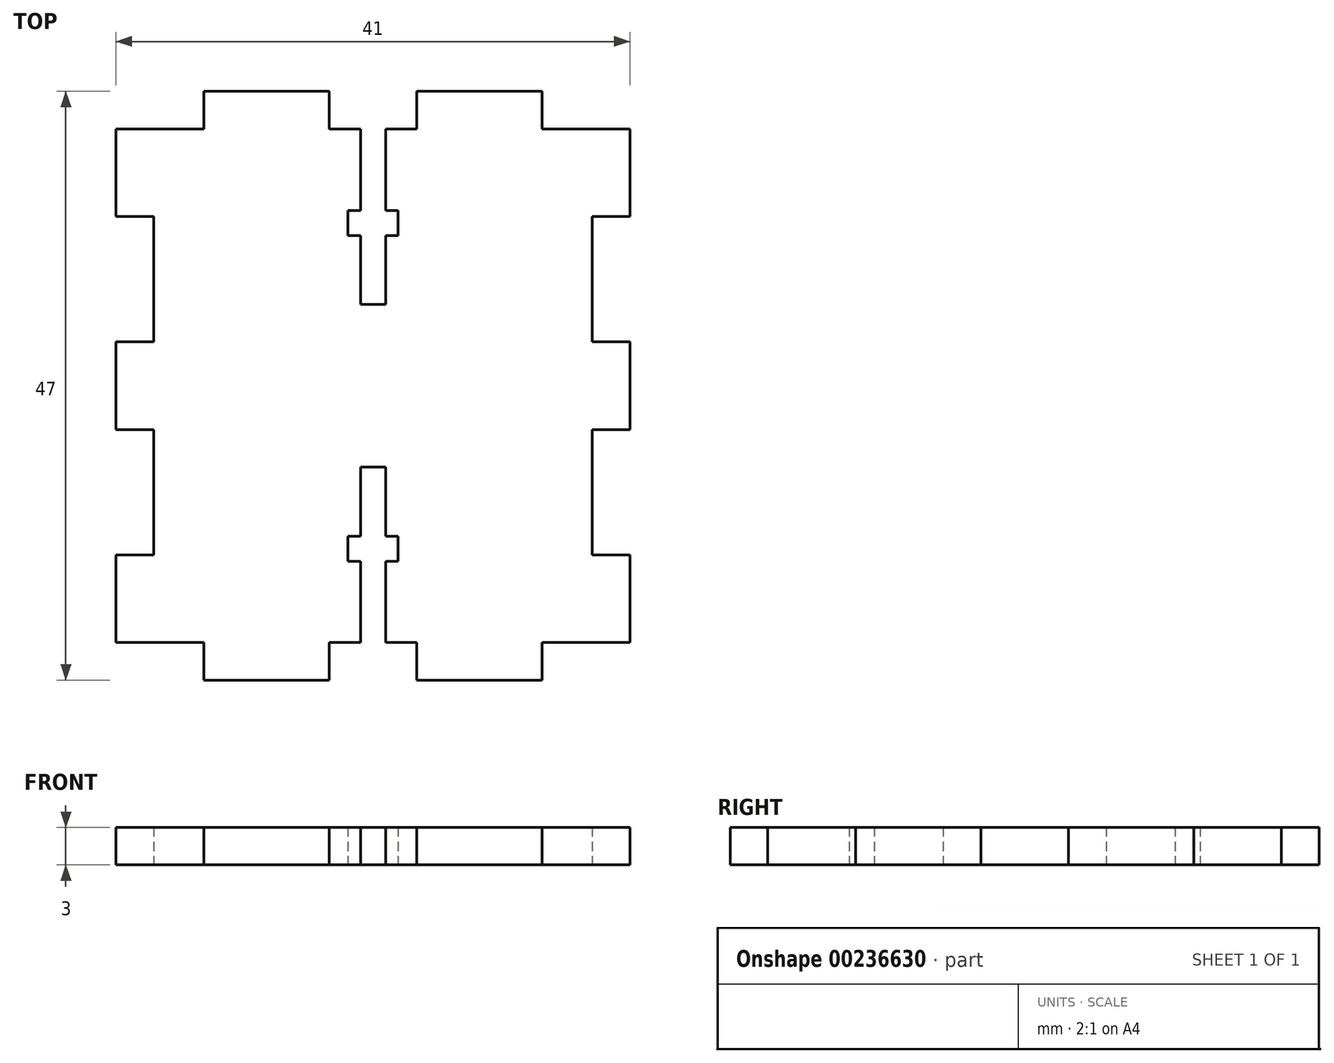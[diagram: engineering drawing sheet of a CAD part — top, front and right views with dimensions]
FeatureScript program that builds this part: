
annotation { "Feature Type Name" : "Feature", "Feature Type Description" : "" }
export const myFeature = defineFeature(function(context is Context, id is Id, definition is map)
    precondition{}
    {
        {
            var Q0;
            Q0=qCreatedBy(makeId("Top.planeOp"),FACE);
            var sketch = newSketch(context, id + "F0", { "sketchPlane" : qUnion([Q0])});
            skLineSegment(sketch, "E0", {"start": v(0, 0) * mm, "end": v(0, 3) * mm});
            skLineSegment(sketch, "E1", {"start": v(0, 3) * mm, "end": v(-7, 3) * mm});
            skLineSegment(sketch, "E2", {"start": v(-7, 3) * mm, "end": v(-7, 10) * mm});
            skLineSegment(sketch, "E3", {"start": v(-7, 10) * mm, "end": v(-4, 10) * mm});
            skLineSegment(sketch, "E4", {"start": v(-4, 10) * mm, "end": v(-4, 20) * mm});
            skLineSegment(sketch, "E5", {"start": v(-4, 20) * mm, "end": v(-7, 20) * mm});
            skLineSegment(sketch, "E6", {"start": v(-7, 20) * mm, "end": v(-7, 27) * mm});
            skLineSegment(sketch, "E7", {"start": v(-7, 27) * mm, "end": v(-4, 27) * mm});
            skLineSegment(sketch, "E8", {"start": v(-4, 27) * mm, "end": v(-4, 37) * mm});
            skLineSegment(sketch, "E9", {"start": v(-4, 37) * mm, "end": v(-7, 37) * mm});
            skLineSegment(sketch, "E10", {"start": v(-7, 37) * mm, "end": v(-7, 44) * mm});
            skLineSegment(sketch, "E11", {"start": v(-7, 44) * mm, "end": v(0, 44) * mm});
            skLineSegment(sketch, "E12", {"start": v(0, 0) * mm, "end": v(10, 0) * mm});
            skLineSegment(sketch, "E13", {"start": v(10, 0) * mm, "end": v(10, 3) * mm});
            skLineSegment(sketch, "E14", {"start": v(0, 44) * mm, "end": v(0, 47) * mm});
            skLineSegment(sketch, "E15", {"start": v(0, 47) * mm, "end": v(10, 47) * mm});
            skLineSegment(sketch, "E16", {"start": v(10, 47) * mm, "end": v(10, 44) * mm});
            skLineSegment(sketch, "E17", {"start": v(10, 44) * mm, "end": v(12.5, 44) * mm});
            skLineSegment(sketch, "E18", {"start": v(10, 3) * mm, "end": v(12.5, 3) * mm});
            skLineSegment(sketch, "E19", {"start": v(12.5, 3) * mm, "end": v(12.5, 9.5) * mm});
            skLineSegment(sketch, "E20", {"start": v(12.5, 9.5) * mm, "end": v(11.5, 9.5) * mm});
            skLineSegment(sketch, "E21", {"start": v(11.5, 9.5) * mm, "end": v(11.5, 11.5) * mm});
            skLineSegment(sketch, "E22", {"start": v(11.5, 11.5) * mm, "end": v(12.5, 11.5) * mm});
            skLineSegment(sketch, "E23", {"start": v(12.5, 11.5) * mm, "end": v(12.5, 17) * mm});
            skLineSegment(sketch, "E24", {"start": v(12.5, 17) * mm, "end": v(14.5, 17) * mm});
            skLineSegment(sketch, "E25", {"start": v(14.5, 17) * mm, "end": v(14.5, 11.5) * mm});
            skLineSegment(sketch, "E26", {"start": v(14.5, 11.5) * mm, "end": v(15.5, 11.5) * mm});
            skLineSegment(sketch, "E27", {"start": v(15.5, 11.5) * mm, "end": v(15.5, 9.5) * mm});
            skLineSegment(sketch, "E28", {"start": v(15.5, 9.5) * mm, "end": v(14.5, 9.5) * mm});
            skLineSegment(sketch, "E29", {"start": v(14.5, 9.5) * mm, "end": v(14.5, 3) * mm});
            skLineSegment(sketch, "E30", {"start": v(14.5, 3) * mm, "end": v(17, 3) * mm});
            skLineSegment(sketch, "E31", {"start": v(12.5, 44) * mm, "end": v(12.5, 37.5) * mm});
            skLineSegment(sketch, "E32", {"start": v(12.5, 37.5) * mm, "end": v(11.5, 37.5) * mm});
            skLineSegment(sketch, "E33", {"start": v(11.5, 37.5) * mm, "end": v(11.5, 35.5) * mm});
            skLineSegment(sketch, "E34", {"start": v(11.5, 35.5) * mm, "end": v(12.5, 35.5) * mm});
            skLineSegment(sketch, "E35", {"start": v(12.5, 35.5) * mm, "end": v(12.5, 30) * mm});
            skLineSegment(sketch, "E36", {"start": v(12.5, 30) * mm, "end": v(14.5, 30) * mm});
            skLineSegment(sketch, "E37", {"start": v(14.5, 30) * mm, "end": v(14.5, 35.5) * mm});
            skLineSegment(sketch, "E38", {"start": v(14.5, 35.5) * mm, "end": v(15.5, 35.5) * mm});
            skLineSegment(sketch, "E39", {"start": v(15.5, 35.5) * mm, "end": v(15.5, 37.5) * mm});
            skLineSegment(sketch, "E40", {"start": v(15.5, 37.5) * mm, "end": v(14.5, 37.5) * mm});
            skLineSegment(sketch, "E41", {"start": v(14.5, 37.5) * mm, "end": v(14.5, 44) * mm});
            skLineSegment(sketch, "E42", {"start": v(14.5, 44) * mm, "end": v(17, 44) * mm});
            skLineSegment(sketch, "E43.MirrorCS", {"start": v(15.5, 35.5) * mm, "end": v(14.5, 35.5) * mm});
            skLineSegment(sketch, "E44.MirrorCS", {"start": v(14.5, 9.5) * mm, "end": v(15.5, 9.5) * mm});
            skLineSegment(sketch, "E45.MirrorCS", {"start": v(11.5, 9.5) * mm, "end": v(12.5, 9.5) * mm});
            skLineSegment(sketch, "E46.MirrorCS", {"start": v(11.5, 37.5) * mm, "end": v(12.5, 37.5) * mm});
            skLineSegment(sketch, "E47.MirrorCS", {"start": v(15.5, 9.5) * mm, "end": v(15.5, 11.5) * mm});
            skLineSegment(sketch, "E48.MirrorCS", {"start": v(15.5, 37.5) * mm, "end": v(15.5, 35.5) * mm});
            skLineSegment(sketch, "E49.MirrorCS", {"start": v(15.5, 11.5) * mm, "end": v(14.5, 11.5) * mm});
            skLineSegment(sketch, "E50.MirrorCS", {"start": v(14.5, 37.5) * mm, "end": v(15.5, 37.5) * mm});
            skLineSegment(sketch, "E51.MirrorCS", {"start": v(17, 47) * mm, "end": v(17, 44) * mm});
            skLineSegment(sketch, "E52.MirrorCS", {"start": v(17, 3) * mm, "end": v(14.5, 3) * mm});
            skLineSegment(sketch, "E53.MirrorCS", {"start": v(14.5, 30) * mm, "end": v(12.5, 30) * mm});
            skLineSegment(sketch, "E54.MirrorCS", {"start": v(12.5, 11.5) * mm, "end": v(11.5, 11.5) * mm});
            skLineSegment(sketch, "E55.MirrorCS", {"start": v(14.5, 17) * mm, "end": v(12.5, 17) * mm});
            skLineSegment(sketch, "E56.MirrorCS", {"start": v(17, 44) * mm, "end": v(14.5, 44) * mm});
            skLineSegment(sketch, "E57.MirrorCS", {"start": v(17, 0) * mm, "end": v(17, 3) * mm});
            skLineSegment(sketch, "E58.MirrorCS", {"start": v(27, 44) * mm, "end": v(27, 47) * mm});
            skLineSegment(sketch, "E59.MirrorCS", {"start": v(27, 0) * mm, "end": v(27, 3) * mm});
            skLineSegment(sketch, "E60.MirrorCS", {"start": v(34, 10) * mm, "end": v(31, 10) * mm});
            skLineSegment(sketch, "E61.MirrorCS", {"start": v(31, 20) * mm, "end": v(34, 20) * mm});
            skLineSegment(sketch, "E62.MirrorCS", {"start": v(34, 27) * mm, "end": v(31, 27) * mm});
            skLineSegment(sketch, "E63.MirrorCS", {"start": v(31, 37) * mm, "end": v(34, 37) * mm});
            skLineSegment(sketch, "E64.MirrorCS", {"start": v(11.5, 11.5) * mm, "end": v(11.5, 9.5) * mm});
            skLineSegment(sketch, "E65.MirrorCS", {"start": v(11.5, 35.5) * mm, "end": v(11.5, 37.5) * mm});
            skLineSegment(sketch, "E66.MirrorCS", {"start": v(12.5, 35.5) * mm, "end": v(11.5, 35.5) * mm});
            skLineSegment(sketch, "E67.MirrorCS", {"start": v(12.5, 9.5) * mm, "end": v(12.5, 3) * mm});
            skLineSegment(sketch, "E68.MirrorCS", {"start": v(12.5, 44) * mm, "end": v(10, 44) * mm});
            skLineSegment(sketch, "E69.MirrorCS", {"start": v(12.5, 3) * mm, "end": v(10, 3) * mm});
            skLineSegment(sketch, "E70.MirrorCS", {"start": v(12.5, 30) * mm, "end": v(12.5, 35.5) * mm});
            skLineSegment(sketch, "E71.MirrorCS", {"start": v(14.5, 35.5) * mm, "end": v(14.5, 30) * mm});
            skLineSegment(sketch, "E72.MirrorCS", {"start": v(12.5, 37.5) * mm, "end": v(12.5, 44) * mm});
            skLineSegment(sketch, "E73.MirrorCS", {"start": v(14.5, 3) * mm, "end": v(14.5, 9.5) * mm});
            skLineSegment(sketch, "E74.MirrorCS", {"start": v(27, 47) * mm, "end": v(17, 47) * mm});
            skLineSegment(sketch, "E75.MirrorCS", {"start": v(27, 3) * mm, "end": v(34, 3) * mm});
            skLineSegment(sketch, "E76.MirrorCS", {"start": v(34, 3) * mm, "end": v(34, 10) * mm});
            skLineSegment(sketch, "E77.MirrorCS", {"start": v(31, 10) * mm, "end": v(31, 20) * mm});
            skLineSegment(sketch, "E78.MirrorCS", {"start": v(34, 20) * mm, "end": v(34, 27) * mm});
            skLineSegment(sketch, "E79.MirrorCS", {"start": v(31, 27) * mm, "end": v(31, 37) * mm});
            skLineSegment(sketch, "E80.MirrorCS", {"start": v(34, 37) * mm, "end": v(34, 44) * mm});
            skLineSegment(sketch, "E81.MirrorCS", {"start": v(34, 44) * mm, "end": v(27, 44) * mm});
            skLineSegment(sketch, "E82.MirrorCS", {"start": v(27, 0) * mm, "end": v(17, 0) * mm});
            skLineSegment(sketch, "E83.MirrorCS", {"start": v(12.5, 17) * mm, "end": v(12.5, 11.5) * mm});
            skLineSegment(sketch, "E84.MirrorCS", {"start": v(14.5, 11.5) * mm, "end": v(14.5, 17) * mm});
            skLineSegment(sketch, "E85.MirrorCS", {"start": v(14.5, 44) * mm, "end": v(14.5, 37.5) * mm});
            skSolve(sketch);
        }
        {
            var Q0;
            Q0=makeQuery(id+"F0.imprint","IMPRINT",FACE,{"disambiguationData":[TD([[makeQuery(id+"F0.imprint","IMPRINT",EDGE,{"derivedFrom":sQuery(id+"F0.wireOp",EDGE,"E0")}),-1.0]])]});
            extrude(context, id + "F1", {"entities" : qUnion([Q0]), "depth" : 3 * mm});
        }
    });
